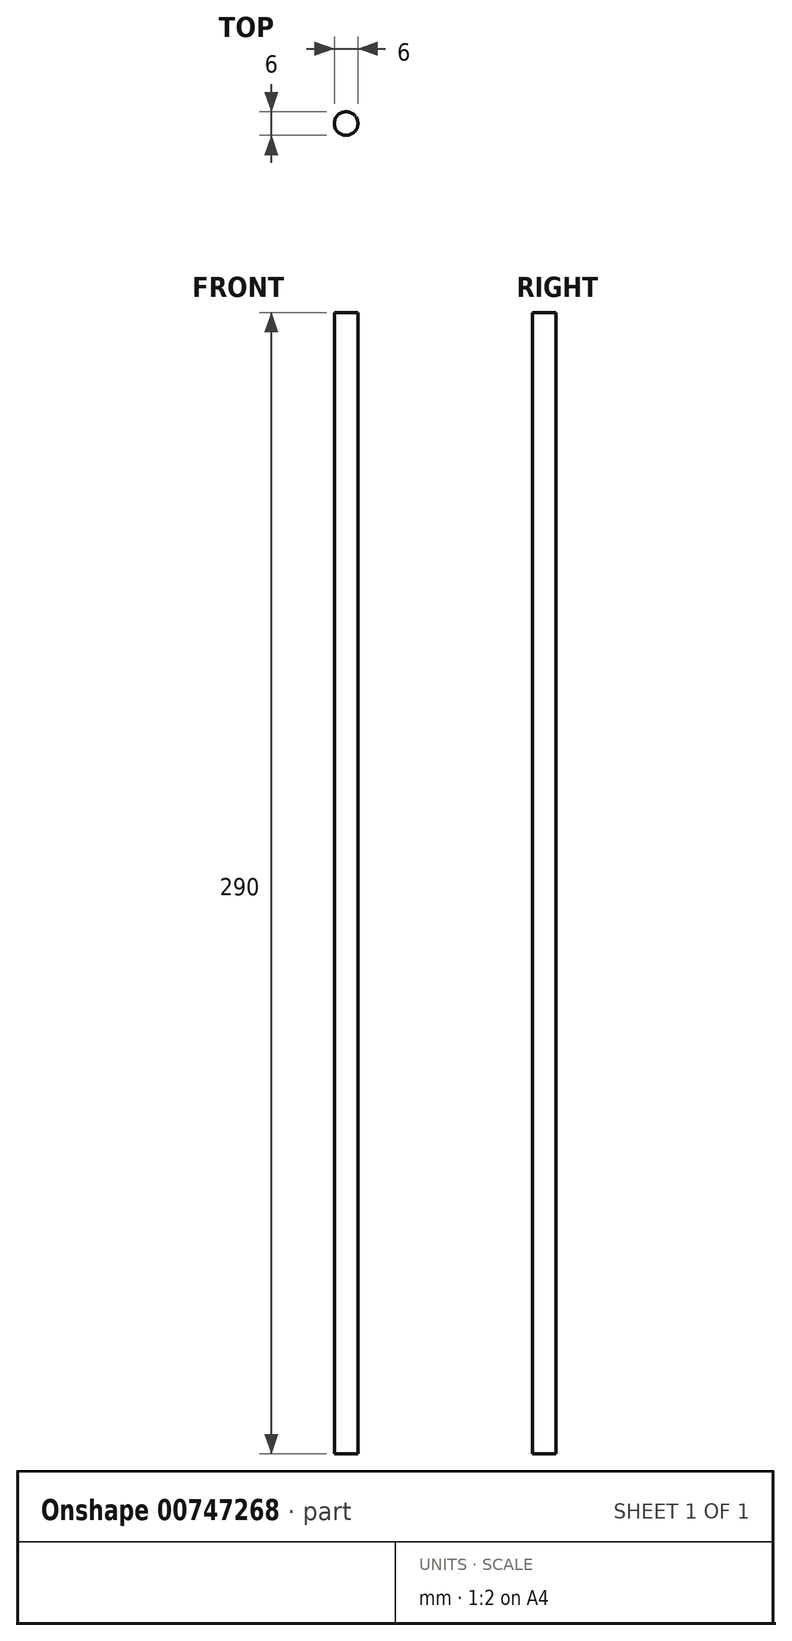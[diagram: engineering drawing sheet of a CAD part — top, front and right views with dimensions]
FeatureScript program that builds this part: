
annotation { "Feature Type Name" : "Feature", "Feature Type Description" : "" }
export const myFeature = defineFeature(function(context is Context, id is Id, definition is map)
    precondition{}
    {
        {
            var Q0;
            Q0=qCreatedBy(makeId("Top.planeOp"),FACE);
            var sketch = newSketch(context, id + "F0", { "sketchPlane" : qUnion([Q0])});
            skCircle(sketch, "E0", {"center": v(0, 0) * mm, "radius": 3 * mm});
            skSolve(sketch);
        }
        {
            var Q0;
            Q0=makeQuery(id+"F0.imprint","IMPRINT",FACE,{"disambiguationData":[TD([[makeQuery(id+"F0.imprint","IMPRINT",EDGE,{"derivedFrom":sQuery(id+"F0.wireOp",EDGE,"E0")}),1.0]])]});
            extrude(context, id + "F1", {"entities" : qUnion([Q0]), "depth" : 290 * mm, "offsetDistance" : 25 * mm});
        }
    });
